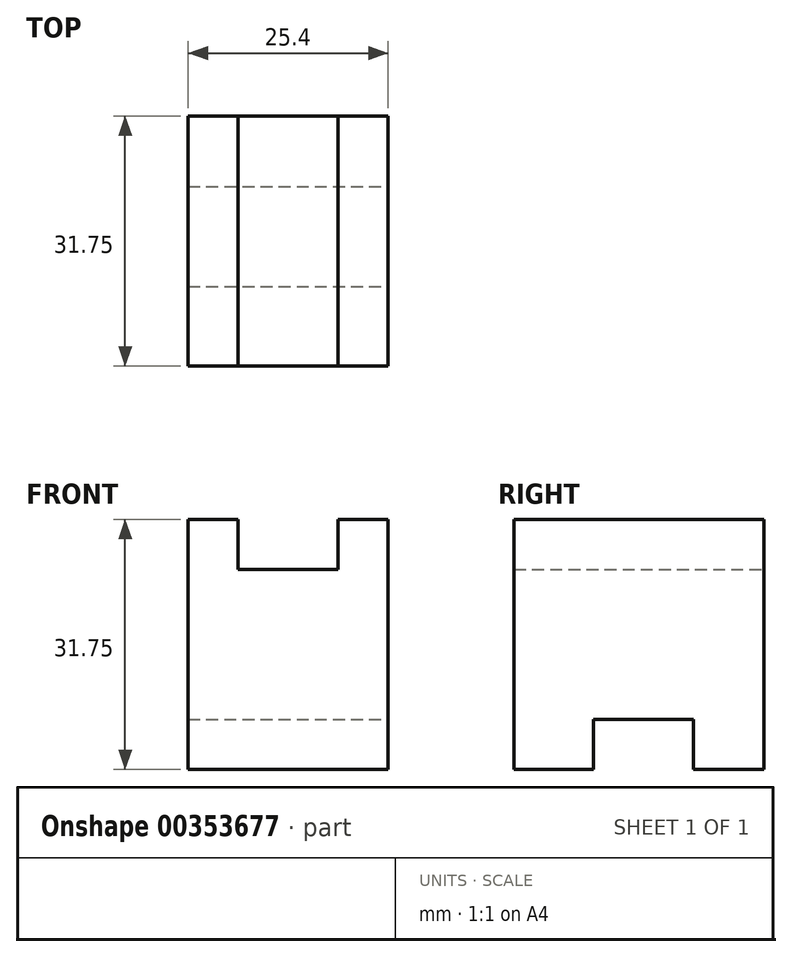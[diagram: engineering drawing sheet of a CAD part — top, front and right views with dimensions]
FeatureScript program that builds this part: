
annotation { "Feature Type Name" : "Feature", "Feature Type Description" : "" }
export const myFeature = defineFeature(function(context is Context, id is Id, definition is map)
    precondition{}
    {
        {
            var Q0;
            Q0=qCreatedBy(makeId("Front.planeOp"),FACE);
            var sketch = newSketch(context, id + "F0", { "sketchPlane" : qUnion([Q0])});
            skLineSegment(sketch, "E0", {"start": v(8.8, 31.75) * mm, "end": v(15.14, 31.75) * mm});
            skLineSegment(sketch, "E1", {"start": v(15.14, 31.75) * mm, "end": v(15.14, 25.4) * mm});
            skLineSegment(sketch, "E2", {"start": v(15.14, 25.4) * mm, "end": v(27.84, 25.4) * mm});
            skLineSegment(sketch, "E3", {"start": v(27.84, 25.4) * mm, "end": v(27.84, 31.75) * mm});
            skLineSegment(sketch, "E4", {"start": v(27.84, 31.75) * mm, "end": v(34.2, 31.75) * mm});
            skLineSegment(sketch, "E5", {"start": v(34.2, 31.75) * mm, "end": v(34.2, 0) * mm});
            skLineSegment(sketch, "E6", {"start": v(8.8, 31.75) * mm, "end": v(8.8, 0) * mm});
            skLineSegment(sketch, "E7", {"start": v(34.2, 0) * mm, "end": v(8.8, 0) * mm});
            skSolve(sketch);
        }
        {
            var Q0;
            Q0=makeQuery(id+"F0.imprint","IMPRINT",FACE,{"disambiguationData":[TD([[makeQuery(id+"F0.imprint","IMPRINT",EDGE,{"derivedFrom":sQuery(id+"F0.wireOp",EDGE,"E0")}),-1.0]])]});
            extrude(context, id + "F1", {"entities" : qUnion([Q0]), "depth" : 31.75 * mm});
        }
        {
            var Q0;
            Q0=makeQuery(id+"F1.opExtrude","SWEPT_FACE",FACE,{"disambiguationData":[OSD([sQuery(id+"F0.wireOp",EDGE,"E5")])]});
            var sketch = newSketch(context, id + "F2", { "sketchPlane" : qUnion([Q0])});
            skLineSegment(sketch, "E8", {"start": v(-21.67, 6.35) * mm, "end": v(-21.67, 0) * mm});
            skLineSegment(sketch, "E9", {"start": v(-21.67, 0) * mm, "end": v(-8.97, 0) * mm});
            skLineSegment(sketch, "E10", {"start": v(-8.97, 0) * mm, "end": v(-8.97, 6.35) * mm});
            skLineSegment(sketch, "E11", {"start": v(-8.97, 6.35) * mm, "end": v(-21.67, 6.35) * mm});
            skSolve(sketch);
        }
        {
            var Q0;
            Q0=makeQuery(id+"F2.imprint","IMPRINT",FACE,{"disambiguationData":[TD([[makeQuery(id+"F2.imprint","IMPRINT",EDGE,{"derivedFrom":sQuery(id+"F2.wireOp",EDGE,"E8")}),1.0]])]});
            extrude(context, id + "F3", {"entities" : qUnion([Q0]), "operationType" : NewBodyOperationType.REMOVE, "oppositeDirection" : true, "depth" : 25.4 * mm});
        }
    });
